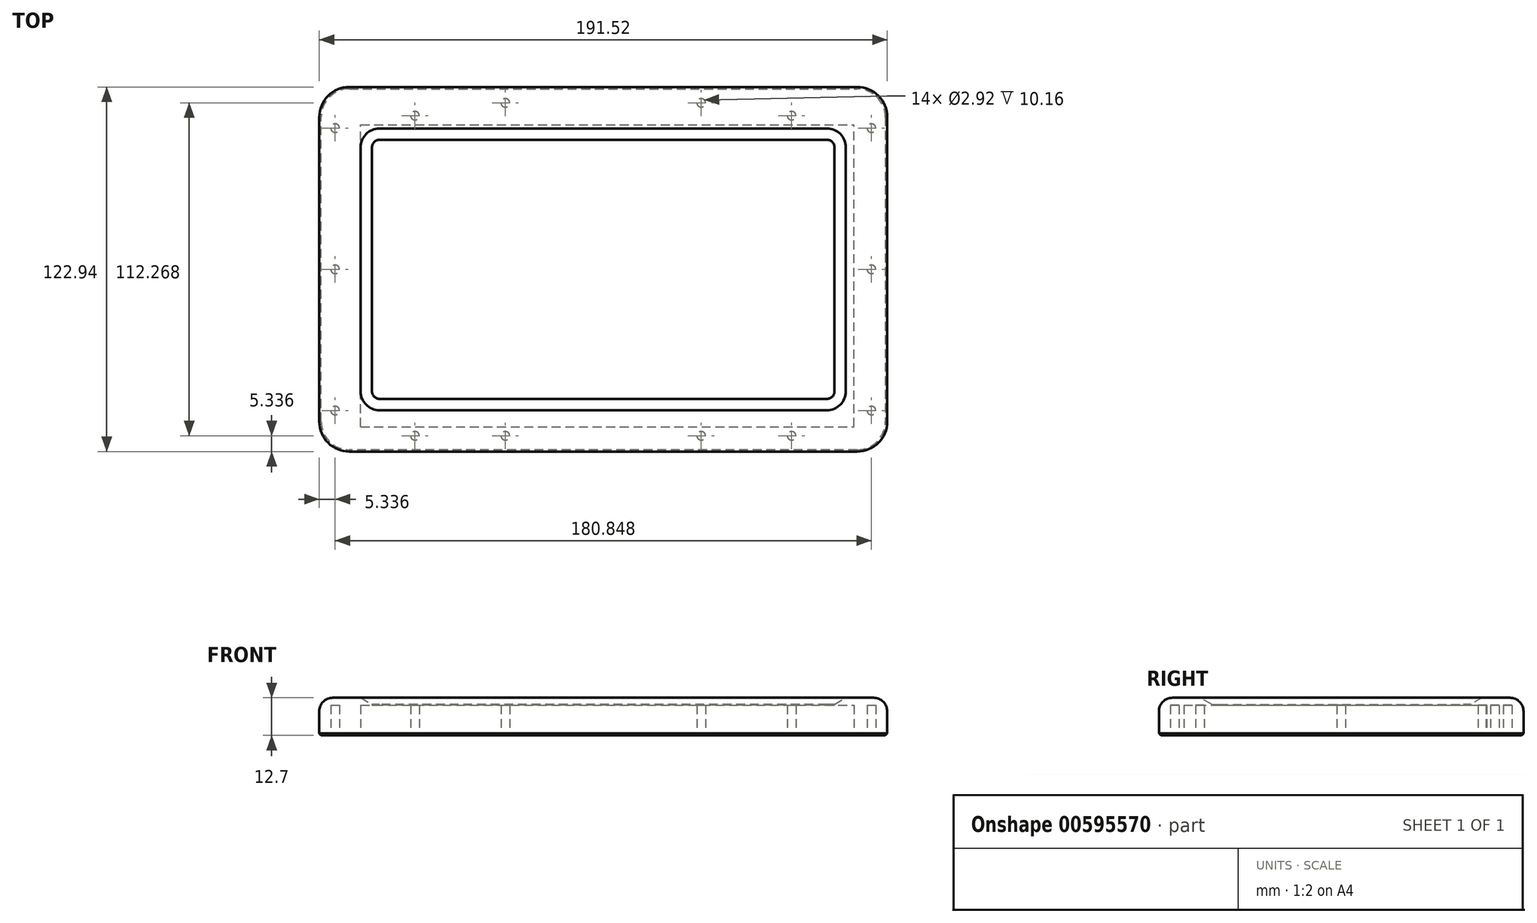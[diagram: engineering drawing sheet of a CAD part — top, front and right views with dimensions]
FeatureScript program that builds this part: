
annotation { "Feature Type Name" : "Feature", "Feature Type Description" : "" }
export const myFeature = defineFeature(function(context is Context, id is Id, definition is map)
    precondition{}
    {
        {
            var Q0;
            Q0=qCreatedBy(makeId("Top.planeOp"),FACE);
            var sketch = newSketch(context, id + "F0", { "sketchPlane" : qUnion([Q0])});
            skLineSegment(sketch, "E0.bottom", {"start": v(-75.44, 43.69) * mm, "end": v(75.44, 43.69) * mm});
            skLineSegment(sketch, "E0.top", {"start": v(-75.44, -43.69) * mm, "end": v(75.44, -43.69) * mm});
            skLineSegment(sketch, "E0.left", {"start": v(-77.98, 41.15) * mm, "end": v(-77.98, -41.15) * mm});
            skLineSegment(sketch, "E0.right", {"start": v(77.98, 41.15) * mm, "end": v(77.98, -41.15) * mm});
            skPoint(sketch, "E1.visualSharp", {"position": v(-77.98, 43.69) * mm});
            skArc(sketch, "E1.filletArc", {"start": v(-75.44, 43.69) * mm, "mid": v(-77.23, 42.94) * mm, "end": v(-77.98, 41.15) * mm});
            skPoint(sketch, "E2.visualSharp", {"position": v(77.98, 43.69) * mm});
            skArc(sketch, "E2.filletArc", {"start": v(77.98, 41.15) * mm, "mid": v(77.23, 42.94) * mm, "end": v(75.44, 43.69) * mm});
            skPoint(sketch, "E3.visualSharp", {"position": v(-77.98, -43.69) * mm});
            skArc(sketch, "E3.filletArc", {"start": v(-77.98, -41.15) * mm, "mid": v(-77.23, -42.94) * mm, "end": v(-75.44, -43.69) * mm});
            skPoint(sketch, "E4.visualSharp", {"position": v(77.98, -43.69) * mm});
            skArc(sketch, "E4.filletArc", {"start": v(75.44, -43.69) * mm, "mid": v(77.23, -42.94) * mm, "end": v(77.98, -41.15) * mm});
            skLineSegment(sketch, "E5", {"start": v(-64.3, 30.01) * mm, "end": v(-94.74, 60.45) * mm, "construction": true});
            skLineSegment(sketch, "E6.bottom", {"start": v(-85.6, 61.47) * mm, "end": v(85.6, 61.47) * mm});
            skLineSegment(sketch, "E6.top", {"start": v(-85.6, -61.47) * mm, "end": v(85.6, -61.47) * mm});
            skLineSegment(sketch, "E6.left", {"start": v(-95.76, 51.3) * mm, "end": v(-95.76, -51.3) * mm});
            skLineSegment(sketch, "E6.right", {"start": v(95.76, 51.3) * mm, "end": v(95.76, -51.3) * mm});
            skPoint(sketch, "E7.visualSharp", {"position": v(-95.76, 61.47) * mm});
            skArc(sketch, "E7.filletArc", {"start": v(-85.6, 61.47) * mm, "mid": v(-92.78, 58.5) * mm, "end": v(-95.76, 51.3) * mm});
            skPoint(sketch, "E8.visualSharp", {"position": v(95.76, 61.47) * mm});
            skArc(sketch, "E8.filletArc", {"start": v(95.76, 51.3) * mm, "mid": v(92.78, 58.5) * mm, "end": v(85.6, 61.47) * mm});
            skPoint(sketch, "E9.visualSharp", {"position": v(95.76, -61.47) * mm});
            skArc(sketch, "E9.filletArc", {"start": v(85.6, -61.47) * mm, "mid": v(92.78, -58.5) * mm, "end": v(95.76, -51.3) * mm});
            skPoint(sketch, "E10.visualSharp", {"position": v(-95.76, -61.47) * mm});
            skArc(sketch, "E10.filletArc", {"start": v(-95.76, -51.3) * mm, "mid": v(-92.78, -58.5) * mm, "end": v(-85.6, -61.47) * mm});
            skSolve(sketch);
        }
        {
            var Q0;
            Q0 = qSketchRegion(id + "F0", true);
            extrude(context, id + "F1", {"entities" : qUnion([Q0]), "depth" : 12.7 * mm, "offsetDistance" : 25.4 * mm});
        }
        {
            var Q0;
            Q0=makeQuery(id+"F1.opExtrude","CAP_FACE",FACE,{"disambiguationData":[OSD([sQuery(id+"F0.wireOp",EDGE,"E0.bottom"),sQuery(id+"F0.wireOp",EDGE,"E0.top"),sQuery(id+"F0.wireOp",EDGE,"E0.left"),sQuery(id+"F0.wireOp",EDGE,"E0.right"),sQuery(id+"F0.wireOp",EDGE,"E1.filletArc"),sQuery(id+"F0.wireOp",EDGE,"E2.filletArc"),sQuery(id+"F0.wireOp",EDGE,"E3.filletArc"),sQuery(id+"F0.wireOp",EDGE,"E4.filletArc"),sQuery(id+"F0.wireOp",EDGE,"E6.bottom"),sQuery(id+"F0.wireOp",EDGE,"E6.top"),sQuery(id+"F0.wireOp",EDGE,"E6.left"),sQuery(id+"F0.wireOp",EDGE,"E6.right"),sQuery(id+"F0.wireOp",EDGE,"E7.filletArc"),sQuery(id+"F0.wireOp",EDGE,"E8.filletArc"),sQuery(id+"F0.wireOp",EDGE,"E9.filletArc"),sQuery(id+"F0.wireOp",EDGE,"E10.filletArc")])],"isStart":true});
            var sketch = newSketch(context, id + "F2", { "sketchPlane" : qUnion([Q0])});
            skLineSegment(sketch, "E11.bottom", {"start": v(-81.79, 53.09) * mm, "end": v(84.58, 53.09) * mm});
            skLineSegment(sketch, "E11.top", {"start": v(-81.79, -48.77) * mm, "end": v(84.58, -48.77) * mm});
            skLineSegment(sketch, "E11.left", {"start": v(-81.79, 53.09) * mm, "end": v(-81.79, -48.77) * mm});
            skLineSegment(sketch, "E11.right", {"start": v(84.58, 53.09) * mm, "end": v(84.58, -48.77) * mm});
            skSolve(sketch);
        }
        {
            var Q0;
            Q0 = qSketchRegion(id + "F2", true);
            extrude(context, id + "F3", {"entities" : qUnion([Q0]), "operationType" : NewBodyOperationType.REMOVE, "oppositeDirection" : true, "depth" : 10.16 * mm, "offsetDistance" : 25.4 * mm});
        }
        {
            var Q0;
            Q0=makeQuery(id+"F1.opExtrude","CAP_EDGE",EDGE,{"disambiguationData":[OSD([sQuery(id+"F0.wireOp",EDGE,"E0.top")])],"isStart":false});
            chamfer(context, id + "F4", {"entities" : qUnion([Q0]), "chamferType" : ChamferType.TWO_OFFSETS, "width1" : 2.3 * mm, "oppositeDirection" : false, "width2" : 3.8 * mm, "tangentPropagation" : true});
        }
        {
            var Q0;
            Q0=makeQuery(id+"F1.opExtrude","CAP_EDGE",EDGE,{"disambiguationData":[OSD([sQuery(id+"F0.wireOp",EDGE,"E6.top")])],"isStart":false});
            fillet(context, id + "F5", {"entities" : qUnion([Q0]), "radius" : 4.57 * mm, "tangentPropagation" : true, "allowEdgeOverflow" : false});
        }
        {
            var Q0;
            Q0=makeQuery(id+"F1.opExtrude","CAP_FACE",FACE,{"disambiguationData":[OSD([sQuery(id+"F0.wireOp",EDGE,"E0.bottom"),sQuery(id+"F0.wireOp",EDGE,"E0.top"),sQuery(id+"F0.wireOp",EDGE,"E0.left"),sQuery(id+"F0.wireOp",EDGE,"E0.right"),sQuery(id+"F0.wireOp",EDGE,"E1.filletArc"),sQuery(id+"F0.wireOp",EDGE,"E2.filletArc"),sQuery(id+"F0.wireOp",EDGE,"E3.filletArc"),sQuery(id+"F0.wireOp",EDGE,"E4.filletArc"),sQuery(id+"F0.wireOp",EDGE,"E6.bottom"),sQuery(id+"F0.wireOp",EDGE,"E6.top"),sQuery(id+"F0.wireOp",EDGE,"E6.left"),sQuery(id+"F0.wireOp",EDGE,"E6.right"),sQuery(id+"F0.wireOp",EDGE,"E7.filletArc"),sQuery(id+"F0.wireOp",EDGE,"E8.filletArc"),sQuery(id+"F0.wireOp",EDGE,"E9.filletArc"),sQuery(id+"F0.wireOp",EDGE,"E10.filletArc")])],"isStart":true});
            var sketch = newSketch(context, id + "F6", { "sketchPlane" : qUnion([Q0])});
            skLineSegment(sketch, "E12.bottom", {"start": v(63.5, -51.82) * mm, "end": v(-63.5, -51.82) * mm, "construction": true});
            skLineSegment(sketch, "E12.top", {"start": v(63.5, 56.13) * mm, "end": v(-63.5, 56.13) * mm, "construction": true});
            skLineSegment(sketch, "E12.left", {"start": v(63.5, -51.82) * mm, "end": v(63.5, 56.13) * mm, "construction": true});
            skLineSegment(sketch, "E12.right", {"start": v(-63.5, -51.82) * mm, "end": v(-63.5, 56.13) * mm, "construction": true});
            skPoint(sketch, "E12.middle", {"position": v(0, 2.16) * mm});
            skLineSegment(sketch, "E13.bottom", {"start": v(90.42, -47.63) * mm, "end": v(-90.42, -47.63) * mm, "construction": true});
            skLineSegment(sketch, "E13.top", {"start": v(90.42, 47.63) * mm, "end": v(-90.42, 47.63) * mm, "construction": true});
            skLineSegment(sketch, "E13.left", {"start": v(90.42, -47.63) * mm, "end": v(90.42, 47.63) * mm, "construction": true});
            skLineSegment(sketch, "E13.right", {"start": v(-90.42, -47.63) * mm, "end": v(-90.42, 47.63) * mm, "construction": true});
            skPoint(sketch, "E13.middle", {"position": v(0, 0) * mm});
            skCircle(sketch, "E14", {"center": v(-63.5, 56.13) * mm, "radius": 1.46 * mm});
            skCircle(sketch, "E15", {"center": v(63.5, 56.13) * mm, "radius": 1.46 * mm});
            skCircle(sketch, "E16", {"center": v(-63.5, -51.82) * mm, "radius": 1.46 * mm});
            skCircle(sketch, "E17", {"center": v(63.5, -51.82) * mm, "radius": 1.46 * mm});
            skCircle(sketch, "E18", {"center": v(-90.42, 47.63) * mm, "radius": 1.46 * mm});
            skCircle(sketch, "E19", {"center": v(-90.42, -47.63) * mm, "radius": 1.46 * mm});
            skCircle(sketch, "E20", {"center": v(90.42, -47.63) * mm, "radius": 1.46 * mm});
            skCircle(sketch, "E21", {"center": v(90.42, 47.63) * mm, "radius": 1.46 * mm});
            skCircle(sketch, "E22", {"center": v(-90.42, 0) * mm, "radius": 1.46 * mm});
            skCircle(sketch, "E23", {"center": v(90.42, 0) * mm, "radius": 1.46 * mm});
            skCircle(sketch, "E24", {"center": v(-33.02, 56.13) * mm, "radius": 1.46 * mm});
            skCircle(sketch, "E25", {"center": v(33.02, 56.13) * mm, "radius": 1.46 * mm});
            skCircle(sketch, "E26", {"center": v(-33.02, -56.13) * mm, "radius": 1.46 * mm});
            skCircle(sketch, "E27", {"center": v(33.02, -56.13) * mm, "radius": 1.46 * mm});
            skLineSegment(sketch, "E28.bottom", {"start": v(-33.02, 56.13) * mm, "end": v(33.02, 56.13) * mm, "construction": true});
            skLineSegment(sketch, "E28.top", {"start": v(-33.02, -56.13) * mm, "end": v(33.02, -56.13) * mm, "construction": true});
            skLineSegment(sketch, "E28.left", {"start": v(-33.02, 56.13) * mm, "end": v(-33.02, -56.13) * mm, "construction": true});
            skLineSegment(sketch, "E28.right", {"start": v(33.02, 56.13) * mm, "end": v(33.02, -56.13) * mm, "construction": true});
            skSolve(sketch);
        }
        {
            var Q0;
            Q0 = qSketchRegion(id + "F6", true);
            extrude(context, id + "F7", {"entities" : qUnion([Q0]), "operationType" : NewBodyOperationType.REMOVE, "oppositeDirection" : true, "depth" : 10.16 * mm, "offsetDistance" : 25.4 * mm});
        }
        {
            var Q0;
            Q0=makeQuery(id+"F3.boolean.opBoolean","COPY",EDGE,{"derivedFrom":makeQuery(id+"F3.opExtrude","CAP_EDGE",EDGE,{"disambiguationData":[OSD([sQuery(id+"F2.wireOp",EDGE,"E11.bottom")])],"isStart":true})});
            var Q1;
            Q1=makeQuery(id+"F1.opExtrude","CAP_EDGE",EDGE,{"disambiguationData":[OSD([sQuery(id+"F0.wireOp",EDGE,"E6.top")])],"isStart":true});
            var Q2;
            Q2=makeQuery(id+"F3.boolean.opBoolean","COPY",EDGE,{"derivedFrom":makeQuery(id+"F3.opExtrude","CAP_EDGE",EDGE,{"disambiguationData":[OSD([sQuery(id+"F2.wireOp",EDGE,"E11.left")])],"isStart":true})});
            var Q3;
            Q3=makeQuery(id+"F3.boolean.opBoolean","COPY",EDGE,{"derivedFrom":makeQuery(id+"F3.opExtrude","CAP_EDGE",EDGE,{"disambiguationData":[OSD([sQuery(id+"F2.wireOp",EDGE,"E11.top")])],"isStart":true})});
            var Q4;
            Q4=makeQuery(id+"F3.boolean.opBoolean","COPY",EDGE,{"derivedFrom":makeQuery(id+"F3.opExtrude","CAP_EDGE",EDGE,{"disambiguationData":[OSD([sQuery(id+"F2.wireOp",EDGE,"E11.right")])],"isStart":true})});
            chamfer(context, id + "F8", {"entities" : qUnion([Q0, Q1, Q2, Q3, Q4]), "width" : 0.64 * mm, "tangentPropagation" : true});
        }
    });
